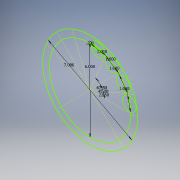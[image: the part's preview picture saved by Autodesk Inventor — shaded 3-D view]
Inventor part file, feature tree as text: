
AUTODESK INVENTOR PART (.ipt)
format: ipt  version: 2016 (Build 200138000, 138)  size: 100,864 bytes
history: native  units: in
note: dims shown in document units (in); Inventor stores cm internally (conversion verified against a paired STEP export)
features: sketch x1
ambient origin geometry x8: Origin, YZ Plane, XZ Plane, XY Plane, X Axis, Y Axis, Z Axis, Center Point
feature tree (1):
  sketch  "Sketch1"  dims[d23=7.0in d24=6.0in d25=45.0deg d26=22.5deg d27=67.5deg d28=1.0in d29=1.0in d30=1.0in d31=1.0in d32=0.2in]
